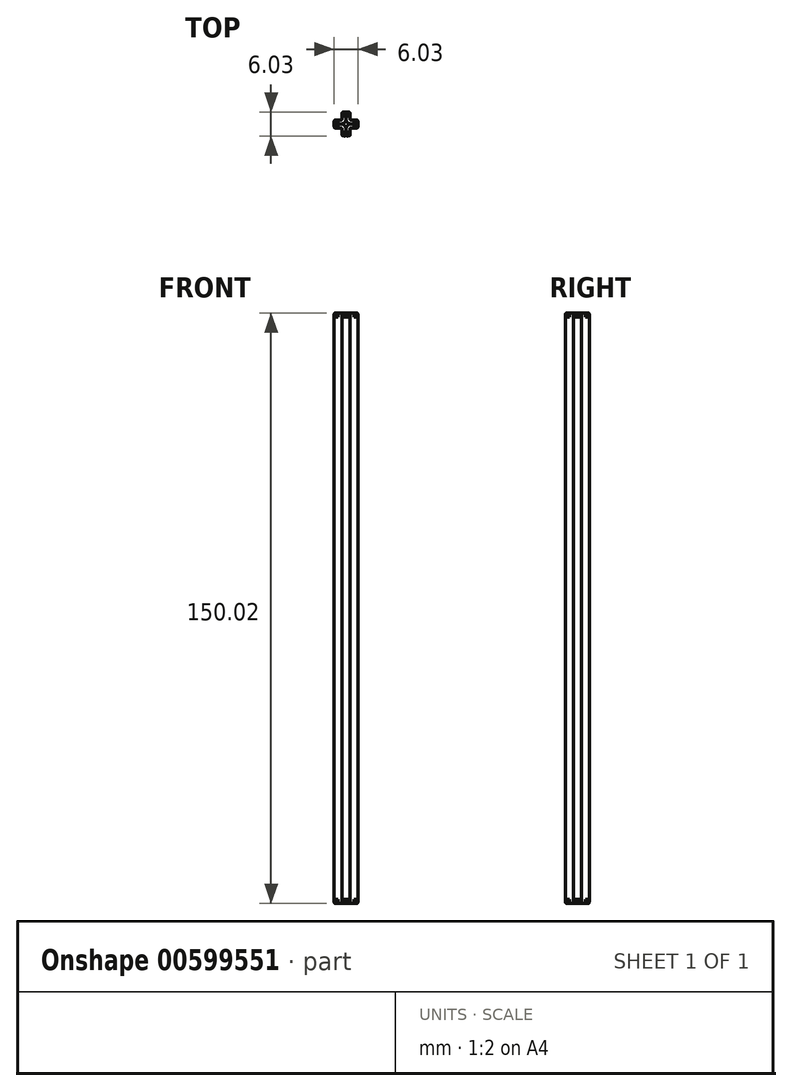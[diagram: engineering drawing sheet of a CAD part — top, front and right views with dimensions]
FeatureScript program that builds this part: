
annotation { "Feature Type Name" : "Feature", "Feature Type Description" : "" }
export const myFeature = defineFeature(function(context is Context, id is Id, definition is map)
    precondition{}
    {
        {
            var Q0;
            Q0=qCreatedBy(makeId("Top.planeOp"),FACE);
            var sketch = newSketch(context, id + "F0", { "sketchPlane" : qUnion([Q0])});
            skLineSegment(sketch, "E0", {"start": v(0.34, -8.55) * mm, "end": v(2.34, -8.55) * mm});
            skLineSegment(sketch, "E1", {"start": v(2.34, -8.55) * mm, "end": v(2.34, -10.55) * mm});
            skLineSegment(sketch, "E2", {"start": v(2.34, -10.55) * mm, "end": v(4.34, -10.55) * mm});
            skLineSegment(sketch, "E3", {"start": v(4.34, -10.55) * mm, "end": v(4.34, -12.55) * mm});
            skLineSegment(sketch, "E4", {"start": v(4.34, -12.55) * mm, "end": v(2.34, -12.55) * mm});
            skLineSegment(sketch, "E5", {"start": v(2.34, -12.55) * mm, "end": v(2.34, -14.55) * mm});
            skLineSegment(sketch, "E6", {"start": v(2.34, -14.55) * mm, "end": v(0.34, -14.55) * mm});
            skLineSegment(sketch, "E7", {"start": v(0.34, -14.55) * mm, "end": v(0.34, -12.55) * mm});
            skLineSegment(sketch, "E8", {"start": v(0.34, -12.55) * mm, "end": v(-1.66, -12.55) * mm});
            skLineSegment(sketch, "E9", {"start": v(-1.66, -12.55) * mm, "end": v(-1.66, -10.55) * mm});
            skLineSegment(sketch, "E10", {"start": v(-1.66, -10.55) * mm, "end": v(0.34, -10.55) * mm});
            skLineSegment(sketch, "E11", {"start": v(0.34, -10.55) * mm, "end": v(0.34, -8.55) * mm});
            skSolve(sketch);
        }
        {
            var Q0;
            Q0=makeQuery(id+"F0.imprint","IMPRINT",FACE,{"disambiguationData":[TD([[makeQuery(id+"F0.imprint","IMPRINT",EDGE,{"derivedFrom":sQuery(id+"F0.wireOp",EDGE,"E0")}),-1.0]])]});
            extrude(context, id + "F1", {"entities" : qUnion([Q0]), "depth" : 150 * mm, "offsetDistance" : 25 * mm});
        }
        {
            var Q0;
            Q0=makeQuery(id+"F1.opExtrude","CAP_FACE",FACE,{"disambiguationData":[OSD([sQuery(id+"F0.wireOp",EDGE,"E0"),sQuery(id+"F0.wireOp",EDGE,"E1"),sQuery(id+"F0.wireOp",EDGE,"E2"),sQuery(id+"F0.wireOp",EDGE,"E3"),sQuery(id+"F0.wireOp",EDGE,"E4"),sQuery(id+"F0.wireOp",EDGE,"E5"),sQuery(id+"F0.wireOp",EDGE,"E6"),sQuery(id+"F0.wireOp",EDGE,"E7"),sQuery(id+"F0.wireOp",EDGE,"E8"),sQuery(id+"F0.wireOp",EDGE,"E9"),sQuery(id+"F0.wireOp",EDGE,"E10"),sQuery(id+"F0.wireOp",EDGE,"E11")])],"isStart":false});
            var Q1;
            Q1=makeQuery(id+"F1.opExtrude","SWEPT_EDGE",EDGE,{"disambiguationData":[OSD([sQuery(id+"F0.wireOp",EDGE,"E0"),sQuery(id+"F0.wireOp",EDGE,"E1")])]});
            var Q2;
            Q2=makeQuery(id+"F1.opExtrude","SWEPT_EDGE",EDGE,{"disambiguationData":[OSD([sQuery(id+"F0.wireOp",EDGE,"E2"),sQuery(id+"F0.wireOp",EDGE,"E3")])]});
            var Q3;
            Q3=makeQuery(id+"F1.opExtrude","SWEPT_EDGE",EDGE,{"disambiguationData":[OSD([sQuery(id+"F0.wireOp",EDGE,"E1"),sQuery(id+"F0.wireOp",EDGE,"E2")])]});
            var Q4;
            Q4=makeQuery(id+"F1.opExtrude","SWEPT_EDGE",EDGE,{"disambiguationData":[OSD([sQuery(id+"F0.wireOp",EDGE,"E3"),sQuery(id+"F0.wireOp",EDGE,"E4")])]});
            var Q5;
            Q5=makeQuery(id+"F1.opExtrude","SWEPT_EDGE",EDGE,{"disambiguationData":[OSD([sQuery(id+"F0.wireOp",EDGE,"E4"),sQuery(id+"F0.wireOp",EDGE,"E5")])]});
            var Q6;
            Q6=makeQuery(id+"F1.opExtrude","SWEPT_EDGE",EDGE,{"disambiguationData":[OSD([sQuery(id+"F0.wireOp",EDGE,"E5"),sQuery(id+"F0.wireOp",EDGE,"E6")])]});
            var Q7;
            Q7=makeQuery(id+"F1.opExtrude","SWEPT_EDGE",EDGE,{"disambiguationData":[OSD([sQuery(id+"F0.wireOp",EDGE,"E6"),sQuery(id+"F0.wireOp",EDGE,"E7")])]});
            var Q8;
            Q8=makeQuery(id+"F1.opExtrude","SWEPT_EDGE",EDGE,{"disambiguationData":[OSD([sQuery(id+"F0.wireOp",EDGE,"E7"),sQuery(id+"F0.wireOp",EDGE,"E8")])]});
            var Q9;
            Q9=makeQuery(id+"F1.opExtrude","SWEPT_EDGE",EDGE,{"disambiguationData":[OSD([sQuery(id+"F0.wireOp",EDGE,"E8"),sQuery(id+"F0.wireOp",EDGE,"E9")])]});
            var Q10;
            Q10=makeQuery(id+"F1.opExtrude","SWEPT_EDGE",EDGE,{"disambiguationData":[OSD([sQuery(id+"F0.wireOp",EDGE,"E9"),sQuery(id+"F0.wireOp",EDGE,"E10")])]});
            var Q11;
            Q11=makeQuery(id+"F1.opExtrude","SWEPT_EDGE",EDGE,{"disambiguationData":[OSD([sQuery(id+"F0.wireOp",EDGE,"E10"),sQuery(id+"F0.wireOp",EDGE,"E11")])]});
            var Q12;
            Q12=makeQuery(id+"F1.opExtrude","CAP_EDGE",EDGE,{"disambiguationData":[OSD([sQuery(id+"F0.wireOp",EDGE,"E3")])],"isStart":true});
            var Q13;
            Q13=makeQuery(id+"F1.opExtrude","CAP_EDGE",EDGE,{"disambiguationData":[OSD([sQuery(id+"F0.wireOp",EDGE,"E6")])],"isStart":true});
            var Q14;
            Q14=makeQuery(id+"F1.opExtrude","SWEPT_EDGE",EDGE,{"disambiguationData":[OSD([sQuery(id+"F0.wireOp",EDGE,"E0"),sQuery(id+"F0.wireOp",EDGE,"E11")])]});
            var Q15;
            Q15=makeQuery(id+"F1.opExtrude","CAP_FACE",FACE,{"disambiguationData":[OSD([sQuery(id+"F0.wireOp",EDGE,"E0"),sQuery(id+"F0.wireOp",EDGE,"E1"),sQuery(id+"F0.wireOp",EDGE,"E2"),sQuery(id+"F0.wireOp",EDGE,"E3"),sQuery(id+"F0.wireOp",EDGE,"E4"),sQuery(id+"F0.wireOp",EDGE,"E5"),sQuery(id+"F0.wireOp",EDGE,"E6"),sQuery(id+"F0.wireOp",EDGE,"E7"),sQuery(id+"F0.wireOp",EDGE,"E8"),sQuery(id+"F0.wireOp",EDGE,"E9"),sQuery(id+"F0.wireOp",EDGE,"E10"),sQuery(id+"F0.wireOp",EDGE,"E11")])],"isStart":true});
            fillet(context, id + "F2", {"entities" : qUnion([Q0, Q1, Q2, Q3, Q4, Q5, Q6, Q7, Q8, Q9, Q10, Q11, Q12, Q13, Q14, Q15]), "radius" : 1 * mm, "rho" : 0.85, "crossSection" : FilletCrossSection.CONIC, "allowEdgeOverflow" : false});
        }
    });
